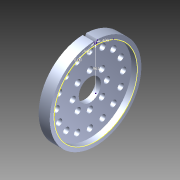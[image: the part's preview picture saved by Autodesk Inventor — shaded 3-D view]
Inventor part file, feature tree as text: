
AUTODESK INVENTOR PART (.ipt)
format: ipt  version: 2014 (Build 180170000, 170)  size: 295,936 bytes
history: native  units: in
note: dims shown in document units (in); Inventor stores cm internally (conversion verified against a paired STEP export)
features: other x2, sketch x1, imported_body x1
ambient origin geometry x8: Origin, YZ Plane, XZ Plane, XY Plane, X Axis, Y Axis, Z Axis, Center Point
bodies: Body1 (feature_tree)
feature tree (4):
  other  "9_64 (0.14063) Diameter Hole1"
  other  "User Library-6151941"
  sketch  "Sketch1"  dims[d0=25.1969in d2=0.0in d4=0.4in d5=0.9605in d6=0.4in]
  imported_body  "Base1"
